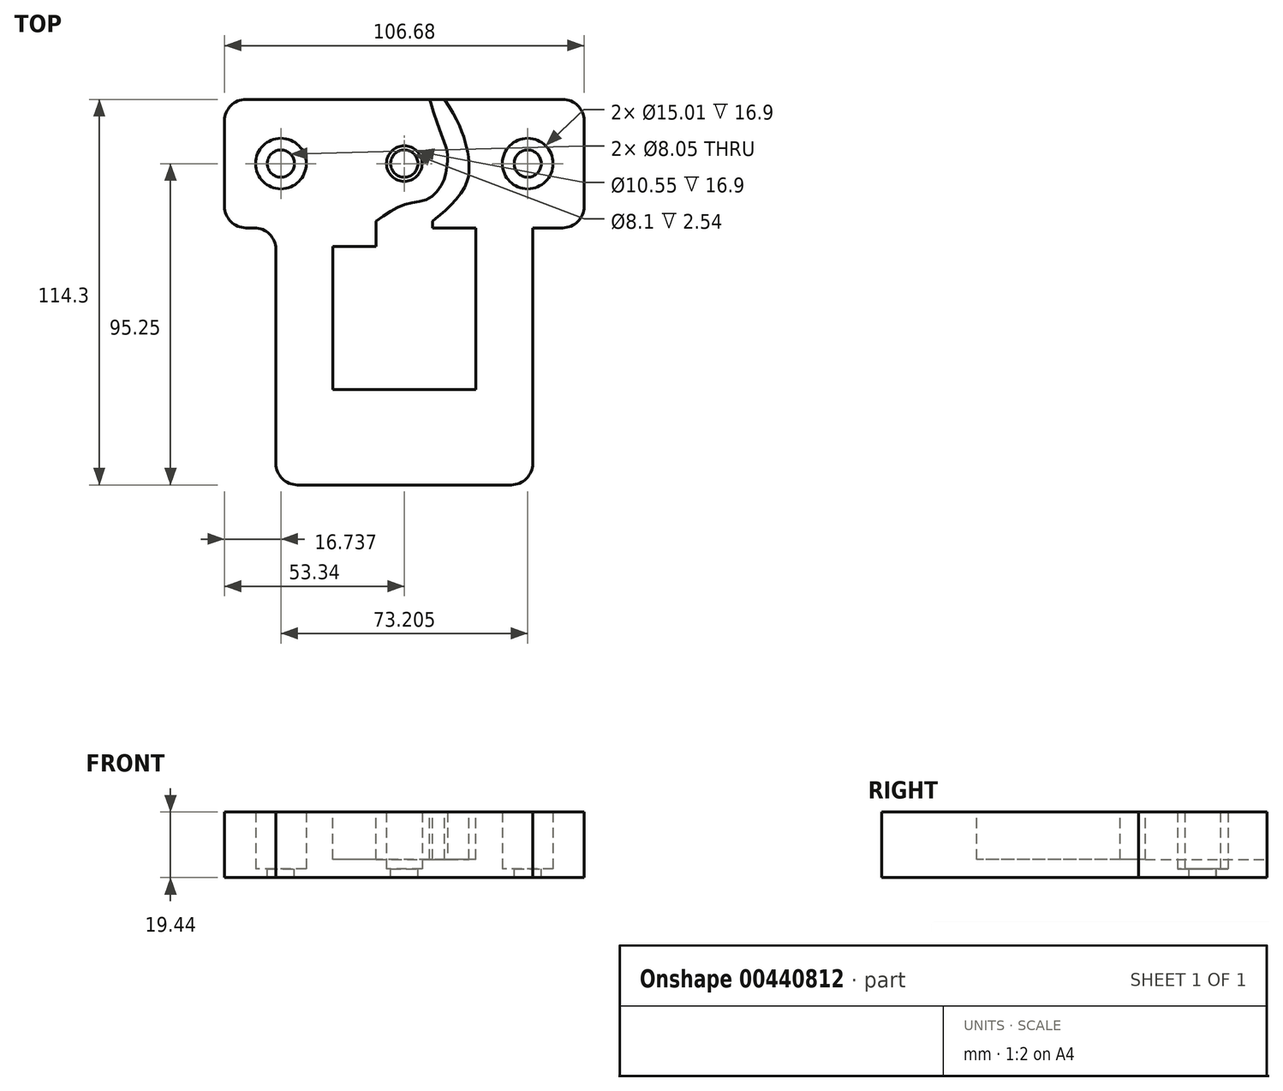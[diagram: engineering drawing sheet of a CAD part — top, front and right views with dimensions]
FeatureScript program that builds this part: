
annotation { "Feature Type Name" : "Feature", "Feature Type Description" : "" }
export const myFeature = defineFeature(function(context is Context, id is Id, definition is map)
    precondition{}
    {
        {
            var Q0;
            Q0=qCreatedBy(makeId("Top.planeOp"),FACE);
            var sketch = newSketch(context, id + "F0", { "sketchPlane" : qUnion([Q0])});
            skPoint(sketch, "E0.middle", {"position": v(-0.19, 0) * mm});
            skCircle(sketch, "E1", {"center": v(0, 0) * mm, "radius": 5.28 * mm});
            skLineSegment(sketch, "E2", {"start": v(0, 0) * mm, "end": v(36.6, 0) * mm});
            skCircle(sketch, "E3", {"center": v(36.6, 0) * mm, "radius": 7.5 * mm});
            skCircle(sketch, "E4.MirrorC", {"center": v(-36.6, 0) * mm, "radius": 7.5 * mm});
            skLineSegment(sketch, "E5.MirrorCS", {"start": v(0, 0) * mm, "end": v(-36.6, 0) * mm});
            skLineSegment(sketch, "E6.bottom", {"start": v(53.34, 19.05) * mm, "end": v(-53.34, 19.05) * mm});
            skLineSegment(sketch, "E6.top", {"start": v(53.34, -19.05) * mm, "end": v(-53.34, -19.05) * mm});
            skLineSegment(sketch, "E6.left", {"start": v(53.34, 19.05) * mm, "end": v(53.34, -19.05) * mm});
            skLineSegment(sketch, "E6.right", {"start": v(-53.34, 19.05) * mm, "end": v(-53.34, -19.05) * mm});
            skSolve(sketch);
        }
        {
            var Q0;
            Q0 = qSketchRegion(id + "F0", true);
            extrude(context, id + "F1", {"entities" : qUnion([Q0]), "depth" : 16.9 * mm});
        }
        {
            var Q0;
            Q0=makeQuery(id+"F1.opExtrude","CAP_FACE",FACE,{"disambiguationData":[OSD([sQuery(id+"F0.wireOp",EDGE,"E1"),sQuery(id+"F0.wireOp",EDGE,"E3"),sQuery(id+"F0.wireOp",EDGE,"E4.MirrorC"),sQuery(id+"F0.wireOp",EDGE,"E6.bottom"),sQuery(id+"F0.wireOp",EDGE,"E6.top"),sQuery(id+"F0.wireOp",EDGE,"E6.left"),sQuery(id+"F0.wireOp",EDGE,"E6.right")])],"isStart":true});
            var sketch = newSketch(context, id + "F2", { "sketchPlane" : qUnion([Q0])});
            skLineSegment(sketch, "E7.bottom", {"start": v(53.34, 19.05) * mm, "end": v(-53.34, 19.05) * mm});
            skLineSegment(sketch, "E7.top", {"start": v(53.34, -19.05) * mm, "end": v(-53.34, -19.05) * mm});
            skLineSegment(sketch, "E7.left", {"start": v(53.34, 19.05) * mm, "end": v(53.34, -19.05) * mm});
            skLineSegment(sketch, "E7.right", {"start": v(-53.34, 19.05) * mm, "end": v(-53.34, -19.05) * mm});
            skPoint(sketch, "E7.middle", {"position": v(0, 0) * mm});
            skCircle(sketch, "E8", {"center": v(-36.6, 0) * mm, "radius": 4.03 * mm});
            skCircle(sketch, "E9.MirrorC", {"center": v(36.6, 0) * mm, "radius": 4.03 * mm});
            skCircle(sketch, "E10", {"center": v(0, 0) * mm, "radius": 4.05 * mm});
            skSolve(sketch);
        }
        {
            var Q0;
            Q0 = qSketchRegion(id + "F2", true);
            extrude(context, id + "F3", {"entities" : qUnion([Q0]), "operationType" : NewBodyOperationType.ADD, "depth" : 2.54 * mm});
        }
        {
            var Q0;
            Q0=makeQuery(id+"F1.opExtrude","CAP_FACE",FACE,{"disambiguationData":[OSD([sQuery(id+"F0.wireOp",EDGE,"E1"),sQuery(id+"F0.wireOp",EDGE,"E3"),sQuery(id+"F0.wireOp",EDGE,"E4.MirrorC"),sQuery(id+"F0.wireOp",EDGE,"E6.bottom"),sQuery(id+"F0.wireOp",EDGE,"E6.top"),sQuery(id+"F0.wireOp",EDGE,"E6.left"),sQuery(id+"F0.wireOp",EDGE,"E6.right")])],"isStart":false});
            var sketch = newSketch(context, id + "F4", { "sketchPlane" : qUnion([Q0])});
            skLineSegment(sketch, "E11", {"start": v(0, -19.05) * mm, "end": v(-38.1, -19.05) * mm});
            skLineSegment(sketch, "E12", {"start": v(0, -19.05) * mm, "end": v(38.1, -19.05) * mm});
            skLineSegment(sketch, "E13.bottom", {"start": v(-38.1, -19.05) * mm, "end": v(38.1, -19.05) * mm});
            skLineSegment(sketch, "E13.top", {"start": v(-38.1, -95.25) * mm, "end": v(38.1, -95.25) * mm});
            skLineSegment(sketch, "E13.left", {"start": v(-38.1, -19.05) * mm, "end": v(-38.1, -95.25) * mm});
            skLineSegment(sketch, "E13.right", {"start": v(38.1, -19.05) * mm, "end": v(38.1, -95.25) * mm});
            skSolve(sketch);
        }
        {
            var Q0;
            Q0 = qSketchRegion(id + "F4", true);
            extrude(context, id + "F5", {"entities" : qUnion([Q0]), "operationType" : NewBodyOperationType.ADD, "oppositeDirection" : true, "depth" : 19.44 * mm});
        }
        {
            var Q0;
            Q0=makeQuery(id+"F5.boolean.opBoolean","MERGE",FACE,{"derivedFrom":[makeQuery(id+"F1.opExtrude","CAP_FACE",FACE,{"disambiguationData":[OSD([sQuery(id+"F0.wireOp",EDGE,"E1"),sQuery(id+"F0.wireOp",EDGE,"E3"),sQuery(id+"F0.wireOp",EDGE,"E4.MirrorC"),sQuery(id+"F0.wireOp",EDGE,"E6.bottom"),sQuery(id+"F0.wireOp",EDGE,"E6.top"),sQuery(id+"F0.wireOp",EDGE,"E6.left"),sQuery(id+"F0.wireOp",EDGE,"E6.right")])],"isStart":false}),makeQuery(id+"F5.opExtrude","CAP_FACE",FACE,{"disambiguationData":[OSD([sQuery(id+"F4.wireOp",EDGE,"E13.bottom"),sQuery(id+"F4.wireOp",EDGE,"E13.top"),sQuery(id+"F4.wireOp",EDGE,"E13.left"),sQuery(id+"F4.wireOp",EDGE,"E13.right")])],"isStart":true})]});
            var sketch = newSketch(context, id + "F6", { "sketchPlane" : qUnion([Q0])});
            skLineSegment(sketch, "E14.bottom", {"start": v(21.25, -24.53) * mm, "end": v(-21.25, -24.53) * mm});
            skLineSegment(sketch, "E14.top", {"start": v(21.25, -67.03) * mm, "end": v(-21.25, -67.03) * mm});
            skLineSegment(sketch, "E14.left", {"start": v(21.25, -24.53) * mm, "end": v(21.25, -67.03) * mm});
            skLineSegment(sketch, "E14.right", {"start": v(-21.25, -24.53) * mm, "end": v(-21.25, -67.03) * mm});
            skPoint(sketch, "E14.middle", {"position": v(0, -45.78) * mm});
            skLineSegment(sketch, "E15.bottom", {"start": v(8.35, -17.03) * mm, "end": v(-8.35, -17.03) * mm});
            skLineSegment(sketch, "E15.top", {"start": v(8.35, -32.03) * mm, "end": v(-8.35, -32.03) * mm});
            skLineSegment(sketch, "E15.left", {"start": v(8.35, -17.03) * mm, "end": v(8.35, -32.03) * mm});
            skLineSegment(sketch, "E15.right", {"start": v(-8.35, -17.03) * mm, "end": v(-8.35, -32.03) * mm});
            skPoint(sketch, "E15.middle", {"position": v(0, -24.53) * mm});
            skFitSpline(sketch, "E16", {"points": [v(-8.35, -17.03) * mm, v(0, -12.15) * mm, v(7.01, -10.5) * mm, v(11.45, -5.55) * mm, v(12.72, 0) * mm, v(12.72, 3.83) * mm, v(11.2, 7.9) * mm, v(7.49, 19.05) * mm, v(7.47, 19.05) * mm], "startDerivative": vector(49.51, 33.43) * mm, "endDerivative": vector(-5.46, 0) * mm});
            skFitSpline(sketch, "E17", {"points": [v(8.35, -17.03) * mm, v(17.28, -8.1) * mm, v(19.19, 0) * mm, v(17.92, 7) * mm, v(11.96, 19.05) * mm], "startDerivative": vector(16.46, 11.4) * mm, "endDerivative": vector(-34.44, 51.68) * mm});
            skLineSegment(sketch, "E18", {"start": v(7.49, 19.05) * mm, "end": v(11.96, 19.05) * mm});
            skLineSegment(sketch, "E19", {"start": v(38.1, -19.05) * mm, "end": v(8.35, -19.05) * mm});
            skLineSegment(sketch, "E20", {"start": v(8.35, -19.05) * mm, "end": v(8.35, -24.53) * mm});
            skLineSegment(sketch, "E21", {"start": v(8.35, -24.53) * mm, "end": v(21.25, -24.53) * mm});
            skLineSegment(sketch, "E22", {"start": v(21.25, -24.53) * mm, "end": v(21.25, -19.05) * mm});
            skLineSegment(sketch, "E23", {"start": v(21.25, -19.05) * mm, "end": v(38.1, -19.05) * mm});
            skSolve(sketch);
        }
        {
            var Q0;
            Q0 = qSketchRegion(id + "F6", true);
            extrude(context, id + "F7", {"entities" : qUnion([Q0]), "operationType" : NewBodyOperationType.REMOVE, "oppositeDirection" : true, "depth" : 14 * mm});
        }
        {
            var Q0;
            Q0=makeQuery(id+"F5.opExtrude","SWEPT_EDGE",EDGE,{"disambiguationData":[OSD([sQuery(id+"F0.wireOp",EDGE,"E6.top"),sQuery(id+"F4.wireOp",EDGE,"E13.bottom"),sQuery(id+"F4.wireOp",EDGE,"E13.left")])]});
            var Q1;
            Q1=makeQuery(id+"F3.boolean.opBoolean","MERGE",EDGE,{"derivedFrom":[makeQuery(id+"F1.opExtrude","SWEPT_EDGE",EDGE,{"disambiguationData":[OSD([sQuery(id+"F0.wireOp",EDGE,"E6.top"),sQuery(id+"F0.wireOp",EDGE,"E6.right")])]}),makeQuery(id+"F3.opExtrude","SWEPT_EDGE",EDGE,{"disambiguationData":[OSD([sQuery(id+"F2.wireOp",EDGE,"E7.bottom"),sQuery(id+"F2.wireOp",EDGE,"E7.right")])]})]});
            var Q2;
            Q2=makeQuery(id+"F3.boolean.opBoolean","MERGE",EDGE,{"derivedFrom":[makeQuery(id+"F1.opExtrude","SWEPT_EDGE",EDGE,{"disambiguationData":[OSD([sQuery(id+"F0.wireOp",EDGE,"E6.bottom"),sQuery(id+"F0.wireOp",EDGE,"E6.right")])]}),makeQuery(id+"F3.opExtrude","SWEPT_EDGE",EDGE,{"disambiguationData":[OSD([sQuery(id+"F2.wireOp",EDGE,"E7.top"),sQuery(id+"F2.wireOp",EDGE,"E7.right")])]})]});
            var Q3;
            Q3=makeQuery(id+"F3.boolean.opBoolean","MERGE",EDGE,{"derivedFrom":[makeQuery(id+"F1.opExtrude","SWEPT_EDGE",EDGE,{"disambiguationData":[OSD([sQuery(id+"F0.wireOp",EDGE,"E6.bottom"),sQuery(id+"F0.wireOp",EDGE,"E6.left")])]}),makeQuery(id+"F3.opExtrude","SWEPT_EDGE",EDGE,{"disambiguationData":[OSD([sQuery(id+"F2.wireOp",EDGE,"E7.top"),sQuery(id+"F2.wireOp",EDGE,"E7.left")])]})]});
            var Q4;
            Q4=makeQuery(id+"F3.boolean.opBoolean","MERGE",EDGE,{"derivedFrom":[makeQuery(id+"F1.opExtrude","SWEPT_EDGE",EDGE,{"disambiguationData":[OSD([sQuery(id+"F0.wireOp",EDGE,"E6.top"),sQuery(id+"F0.wireOp",EDGE,"E6.left")])]}),makeQuery(id+"F3.opExtrude","SWEPT_EDGE",EDGE,{"disambiguationData":[OSD([sQuery(id+"F2.wireOp",EDGE,"E7.bottom"),sQuery(id+"F2.wireOp",EDGE,"E7.left")])]})]});
            var Q5;
            Q5=makeQuery(id+"F5.opExtrude","SWEPT_EDGE",EDGE,{"disambiguationData":[OSD([sQuery(id+"F0.wireOp",EDGE,"E6.top"),sQuery(id+"F4.wireOp",EDGE,"E13.bottom"),sQuery(id+"F4.wireOp",EDGE,"E13.right")])]});
            var Q6;
            Q6=makeQuery(id+"F5.opExtrude","SWEPT_EDGE",EDGE,{"disambiguationData":[OSD([sQuery(id+"F4.wireOp",EDGE,"E13.top"),sQuery(id+"F4.wireOp",EDGE,"E13.left")])]});
            var Q7;
            Q7=makeQuery(id+"F5.opExtrude","SWEPT_EDGE",EDGE,{"disambiguationData":[OSD([sQuery(id+"F4.wireOp",EDGE,"E13.top"),sQuery(id+"F4.wireOp",EDGE,"E13.right")])]});
            fillet(context, id + "F8", {"entities" : qUnion([Q0, Q1, Q2, Q3, Q4, Q5, Q6, Q7]), "radius" : 6.35 * mm, "tangentPropagation" : true, "allowEdgeOverflow" : false});
        }
    });
